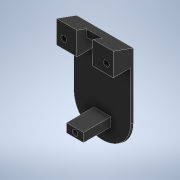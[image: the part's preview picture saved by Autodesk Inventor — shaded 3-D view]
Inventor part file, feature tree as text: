
AUTODESK INVENTOR PART (.ipt)
format: ipt  version: 2021 (Build 250183000, 183)  size: 189,440 bytes
history: native  units: mm
features: sketch x8, extrude x6, chamfer x1, sweep x1, projected_geometry x1
ambient origin geometry x8: Origin, YZ Plane, XZ Plane, XY Plane, X Axis, Y Axis, Z Axis, Center Point
bodies: Solid1 (feature_tree)
feature tree (17):
  extrude  "Extrusion1"  Depth=32.0mm
  sketch  "Sketch2"  dims[d2=12.0mm d3=24.0mm]
  extrude  "Extrusion2"  Depth=24.0mm
  chamfer  "Chamfer1"  Distance=9.8mm
  extrude  "Extrusion4"  Depth=9.8mm
  sketch  "Sketch5"  dims[d11=5.25mm d12=0.0mm d15=9.8mm d16=2.0mm d17=3.490659mm]
  sketch  "Sketch4"  dims[d5=3.2mm d6=9.8mm d7=0.0mm]
  sketch  "3D Sketch1"
  sweep  "Sweep1"
  extrude  "Extrusion5"  Depth=15.4mm
  extrude  "Extrusion6"  Depth=15.4mm
  extrude  "Extrusion7"  Depth=15.4mm
  sketch  "Sketch1"  dims[d0=32.0mm d1=13.0mm]
  sketch  "Sketch3"  dims[d4=5.0mm]
  projected_geometry  "Projected Loop1"
  sketch  "Sketch6"  dims[d18=9.0mm d19=7.0mm]
  sketch  "Sketch7"  dims[d20=4.0mm d21=0.0mm d22=27.2mm d23=3.2mm d25=37.0mm d26=0.0mm d27=0.0mm d28=1.5mm d29=0.0mm d30=0.0mm d31=5.0mm d32=9.5mm d33=15.4mm d34=0.0mm d35=30.0mm d36=2.8mm d37=0.0mm d38=0.0mm]
